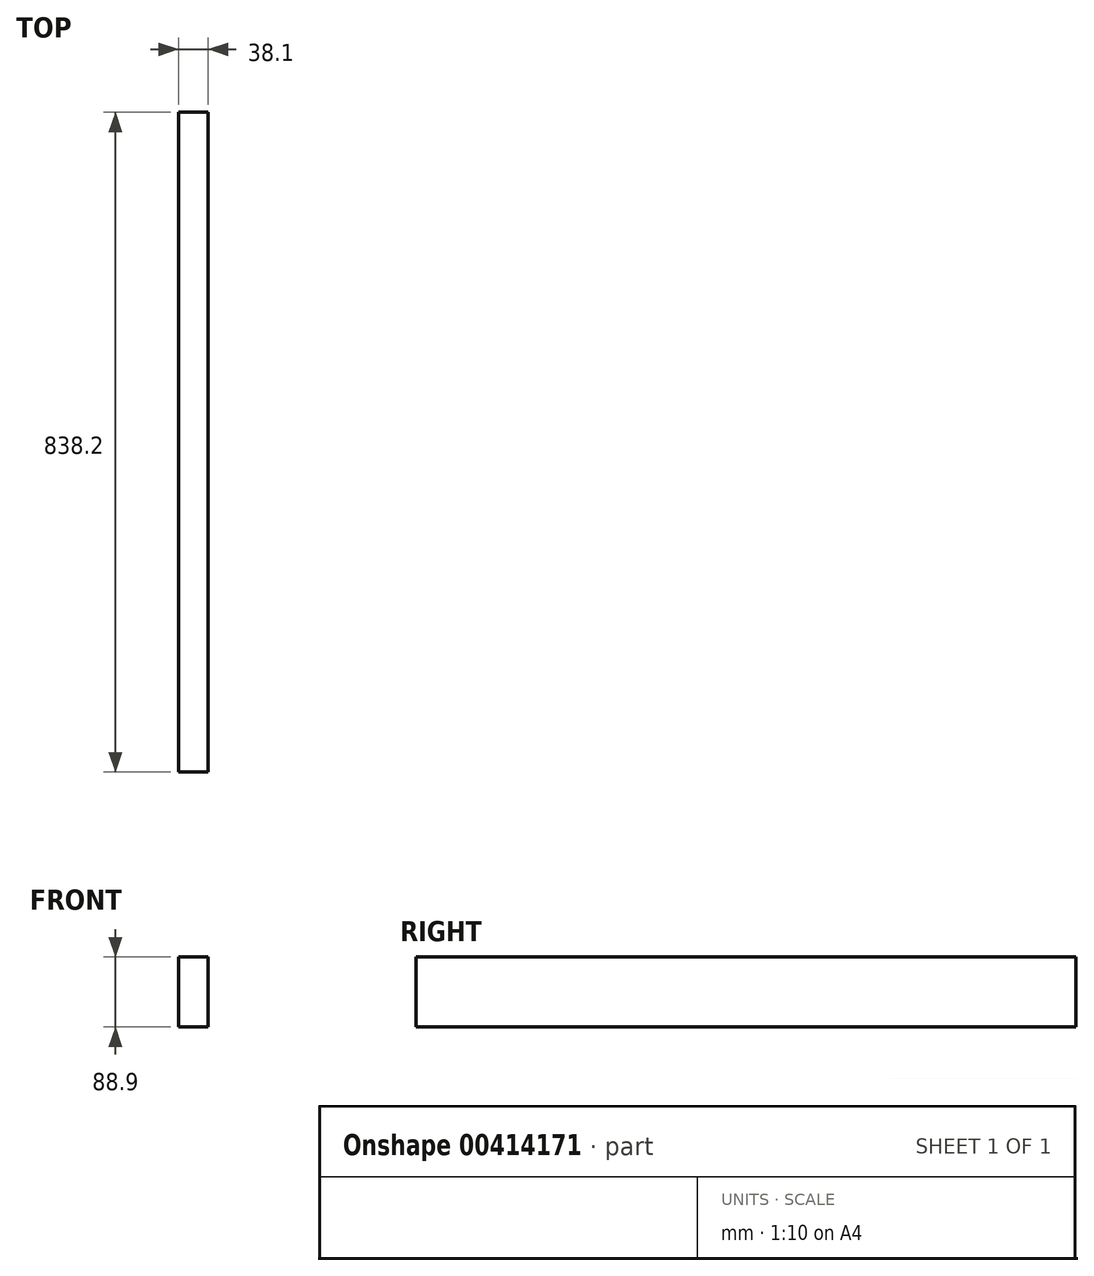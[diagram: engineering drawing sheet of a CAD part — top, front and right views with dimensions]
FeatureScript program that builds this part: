
annotation { "Feature Type Name" : "Feature", "Feature Type Description" : "" }
export const myFeature = defineFeature(function(context is Context, id is Id, definition is map)
    precondition{}
    {
        {
            var Q0;
            Q0=qCreatedBy(makeId("Front.planeOp"),FACE);
            var sketch = newSketch(context, id + "F0", { "sketchPlane" : qUnion([Q0])});
            skLineSegment(sketch, "E0.bottom", {"start": v(19.05, -44.45) * mm, "end": v(-19.05, -44.45) * mm});
            skLineSegment(sketch, "E0.top", {"start": v(19.05, 44.45) * mm, "end": v(-19.05, 44.45) * mm});
            skLineSegment(sketch, "E0.left", {"start": v(19.05, -44.45) * mm, "end": v(19.05, 44.45) * mm});
            skLineSegment(sketch, "E0.right", {"start": v(-19.05, -44.45) * mm, "end": v(-19.05, 44.45) * mm});
            skPoint(sketch, "E0.middle", {"position": v(0, 0) * mm});
            skSolve(sketch);
        }
        {
            var Q0;
            Q0 = qSketchRegion(id + "F0", true);
            extrude(context, id + "F1", {"entities" : qUnion([Q0]), "endBound" : BoundingType.SYMMETRIC, "depth" : 838.2 * mm});
        }
    });
